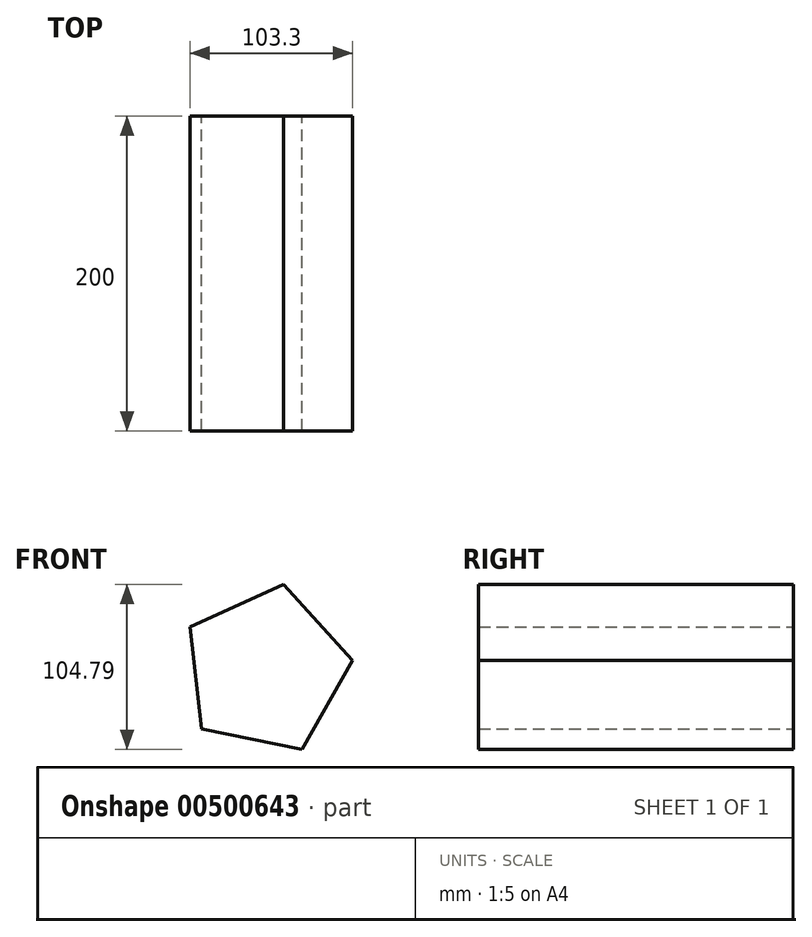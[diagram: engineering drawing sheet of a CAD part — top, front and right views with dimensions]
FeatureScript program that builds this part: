
annotation { "Feature Type Name" : "Feature", "Feature Type Description" : "" }
export const myFeature = defineFeature(function(context is Context, id is Id, definition is map)
    precondition{}
    {
        {
            var Q0;
            Q0=qCreatedBy(makeId("Front.planeOp"),FACE);
            var sketch = newSketch(context, id + "F0", { "sketchPlane" : qUnion([Q0])});
            skCircle(sketch, "E0.cCircle", {"center": v(0, 0) * mm, "radius": 55.44 * mm, "construction": true});
            skLineSegment(sketch, "E0.0", {"start": v(-48.2, 27.4) * mm, "end": v(11.16, 54.3) * mm});
            skLineSegment(sketch, "E0.1", {"start": v(11.16, 54.3) * mm, "end": v(55.1, 6.16) * mm});
            skLineSegment(sketch, "E0.2", {"start": v(55.1, 6.16) * mm, "end": v(22.89, -50.5) * mm});
            skLineSegment(sketch, "E0.3", {"start": v(22.89, -50.5) * mm, "end": v(-40.95, -37.37) * mm});
            skLineSegment(sketch, "E0.4", {"start": v(-40.95, -37.37) * mm, "end": v(-48.2, 27.4) * mm});
            skSolve(sketch);
        }
        {
            var Q0;
            Q0=makeQuery(id+"F0.imprint","IMPRINT",FACE,{"disambiguationData":[TD([[makeQuery(id+"F0.imprint","IMPRINT",EDGE,{"derivedFrom":sQuery(id+"F0.wireOp",EDGE,"E0.0")}),-1.0]])]});
            extrude(context, id + "F1", {"entities" : qUnion([Q0]), "depth" : 200 * mm});
        }
    });
